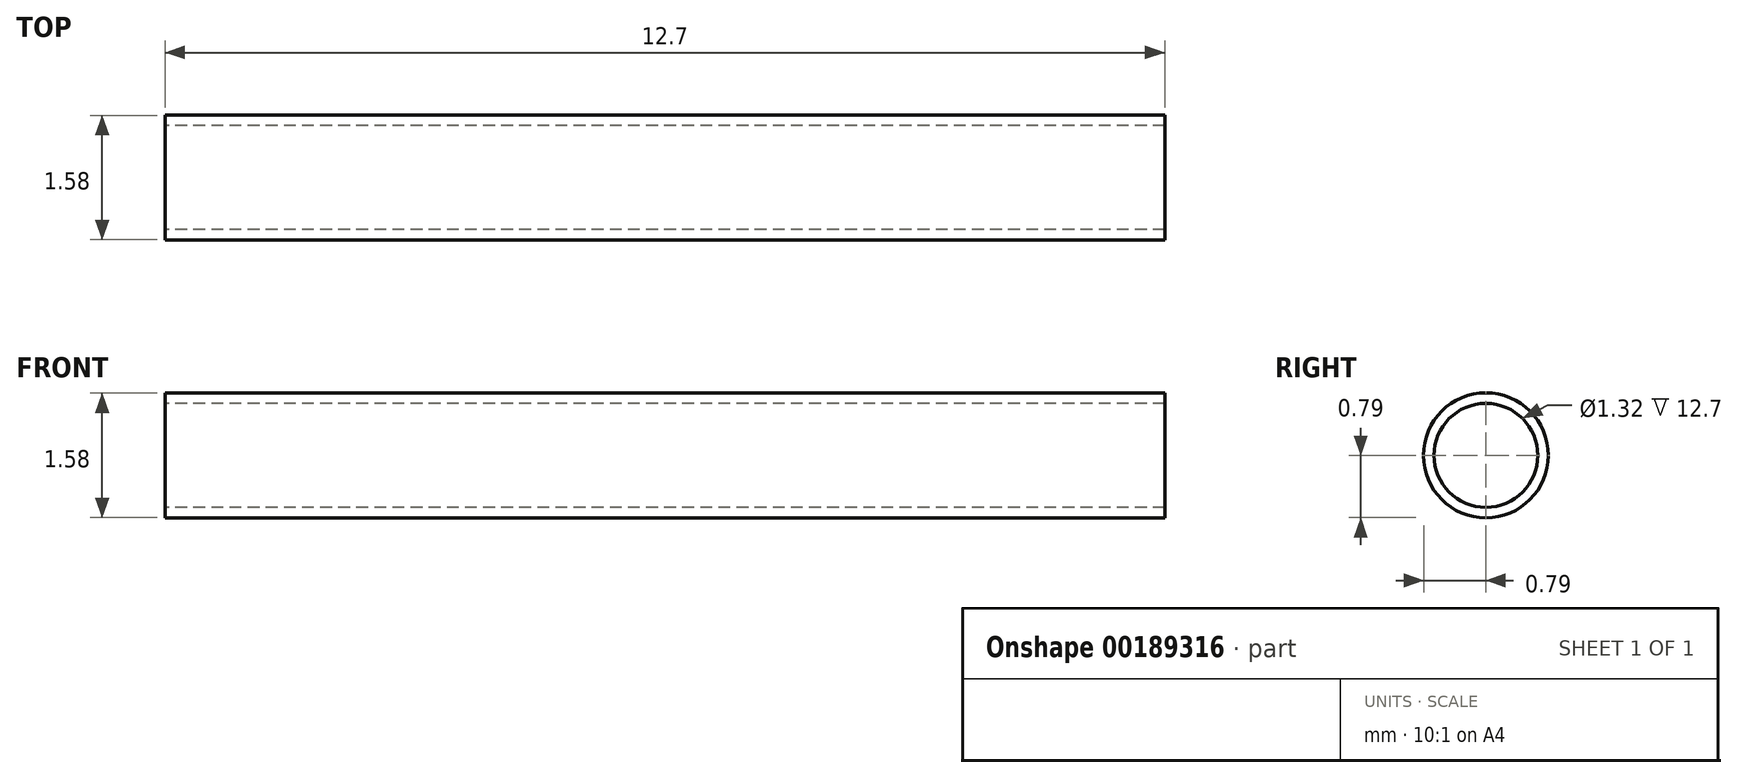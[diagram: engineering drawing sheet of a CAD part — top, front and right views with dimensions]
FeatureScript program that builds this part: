
annotation { "Feature Type Name" : "Feature", "Feature Type Description" : "" }
export const myFeature = defineFeature(function(context is Context, id is Id, definition is map)
    precondition{}
    {
        {
            var Q0;
            Q0=qCreatedBy(makeId("Right.planeOp"),FACE);
            var sketch = newSketch(context, id + "F0", { "sketchPlane" : qUnion([Q0])});
            skCircle(sketch, "E0", {"center": v(0, 0) * mm, "radius": 0.8 * mm});
            skCircle(sketch, "E1", {"center": v(0, 0) * mm, "radius": 0.66 * mm});
            skSolve(sketch);
        }
        {
            var Q0;
            Q0=makeQuery(id+"F0.imprint","IMPRINT",FACE,{"disambiguationData":[TD([[makeQuery(id+"F0.imprint","IMPRINT",EDGE,{"derivedFrom":sQuery(id+"F0.wireOp",EDGE,"E0")}),1.0]])]});
            extrude(context, id + "F1", {"entities" : qUnion([Q0]), "depth" : 12.7 * mm});
        }
    });
